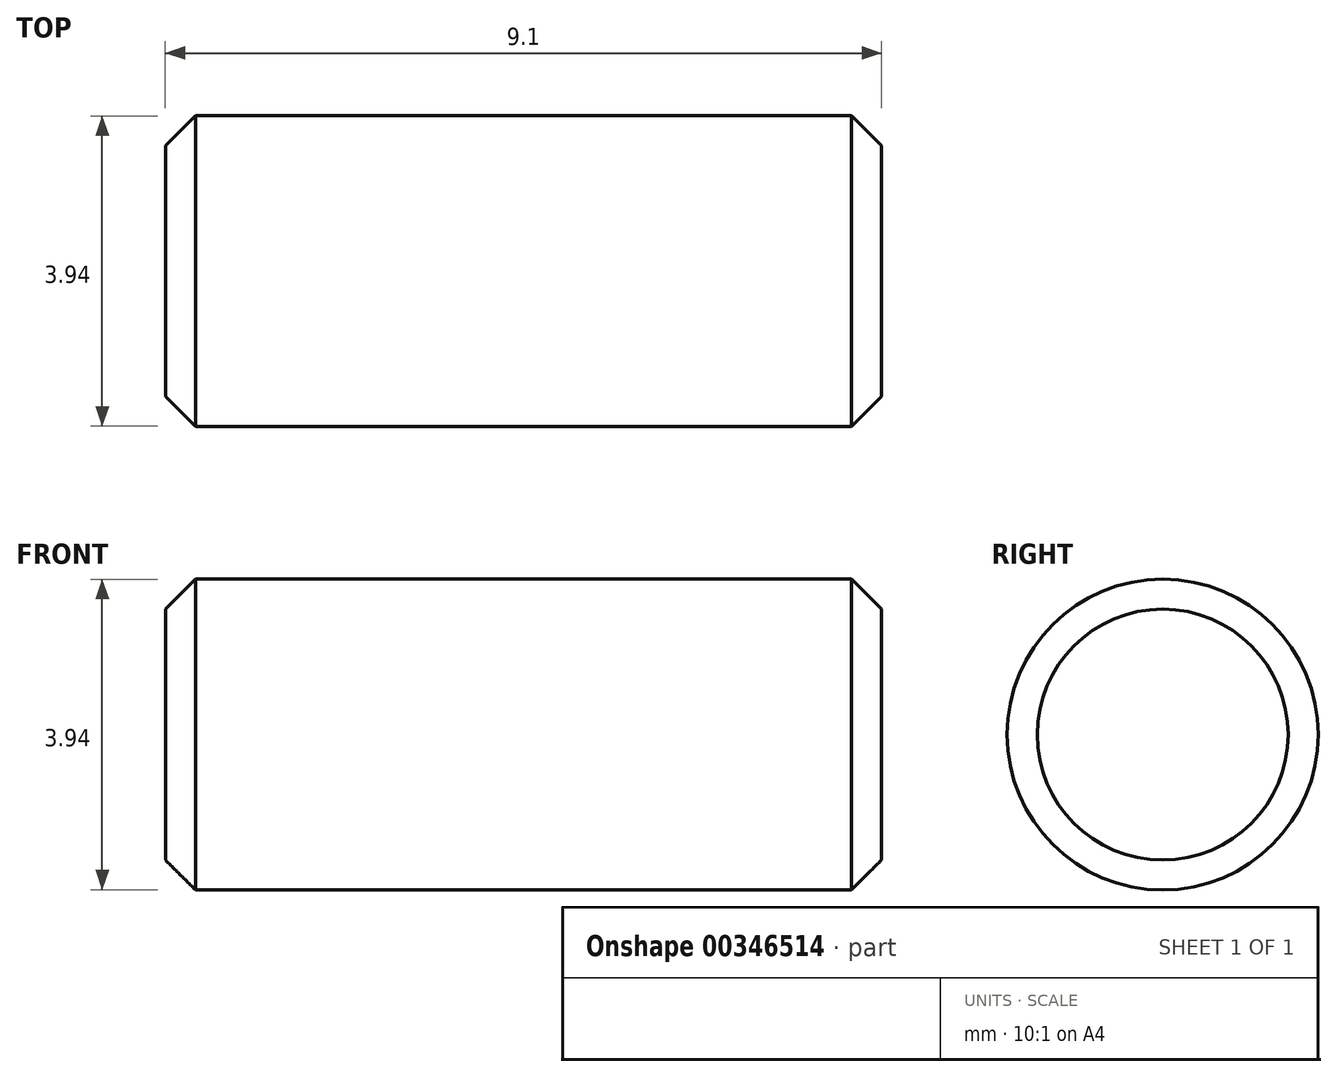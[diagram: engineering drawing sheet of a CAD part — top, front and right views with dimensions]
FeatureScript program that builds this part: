
annotation { "Feature Type Name" : "Feature", "Feature Type Description" : "" }
export const myFeature = defineFeature(function(context is Context, id is Id, definition is map)
    precondition{}
    {
        {
            var Q0;
            Q0=qCreatedBy(makeId("Right.planeOp"),FACE);
            var sketch = newSketch(context, id + "F0", { "sketchPlane" : qUnion([Q0])});
            skCircle(sketch, "E0", {"center": v(0, 0) * mm, "radius": 1.97 * mm});
            skSolve(sketch);
        }
        {
            var Q0;
            Q0=makeQuery(id+"F0.imprint","IMPRINT",FACE,{"disambiguationData":[TD([[makeQuery(id+"F0.imprint","IMPRINT",EDGE,{"derivedFrom":sQuery(id+"F0.wireOp",EDGE,"E0")}),1.0]])]});
            extrude(context, id + "F1", {"entities" : qUnion([Q0]), "depth" : 9.1 * mm, "symmetric" : true});
        }
        {
            var Q0;
            Q0=makeQuery(id+"F1.opExtrude","CAP_EDGE",EDGE,{"disambiguationData":[OSD([sQuery(id+"F0.wireOp",EDGE,"E0")])],"isStart":true});
            var Q1;
            Q1=makeQuery(id+"F1.opExtrude","CAP_EDGE",EDGE,{"disambiguationData":[OSD([sQuery(id+"F0.wireOp",EDGE,"E0")])],"isStart":false});
            chamfer(context, id + "F2", {"entities" : qUnion([Q0, Q1]), "chamferType" : ChamferType.OFFSET_ANGLE, "width" : 0.38 * mm, "oppositeDirection" : false, "angle" : 45 * degree, "tangentPropagation" : true});
        }
    });
